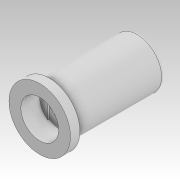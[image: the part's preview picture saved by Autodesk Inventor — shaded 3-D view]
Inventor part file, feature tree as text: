
AUTODESK INVENTOR PART (.ipt)
format: ipt  version: 2020 (Build 240168000, 168)  size: 136,704 bytes
history: native  units: mm
features: sketch x2, revolve x1, fillet x1, extrude x1
ambient origin geometry x8: Origin, YZ Plane, XZ Plane, XY Plane, X Axis, Y Axis, Z Axis, Center Point
bodies: Solid1 (feature_tree)
feature tree (5):
  revolve  "Revolution1"  [1 undecoded]
  fillet  "Fillet1"  Radius=1.0mm
  extrude  "Extrusion1"  Depth=14.5mm
  sketch  "Sketch1"  dims[d0=1.7mm d1=3.9mm d2=1.0mm]
  sketch  "Sketch2"  dims[d3=1.5mm d4=14.5mm d5=90.0deg d6=3.0mm d7=3.0mm d8=0.5mm d9=0.2mm d10=0.0mm]
note: 1 required parameter value undecoded (feature->parameter linkage not recoverable at this tier; creation-order binding heuristic only, values carry confidence <= 0.55)
